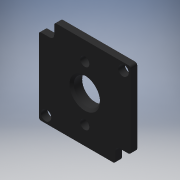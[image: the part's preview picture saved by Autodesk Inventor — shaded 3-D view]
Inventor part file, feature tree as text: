
AUTODESK INVENTOR PART (.ipt)
format: ipt  version: 2016 (Build 200138000, 138)  size: 263,680 bytes
history: native  units: in
note: dims shown in document units (in); Inventor stores cm internally (conversion verified against a paired STEP export)
features: fillet x1
ambient origin geometry x8: Origin, YZ Plane, XZ Plane, XY Plane, X Axis, Y Axis, Z Axis, Center Point
bodies: Solid1 (feature_tree)
feature tree (1):
  fillet  "Fillet4"  [1 undecoded]
note: 1 required parameter value undecoded (feature->parameter linkage not recoverable at this tier; creation-order binding heuristic only, values carry confidence <= 0.55)
